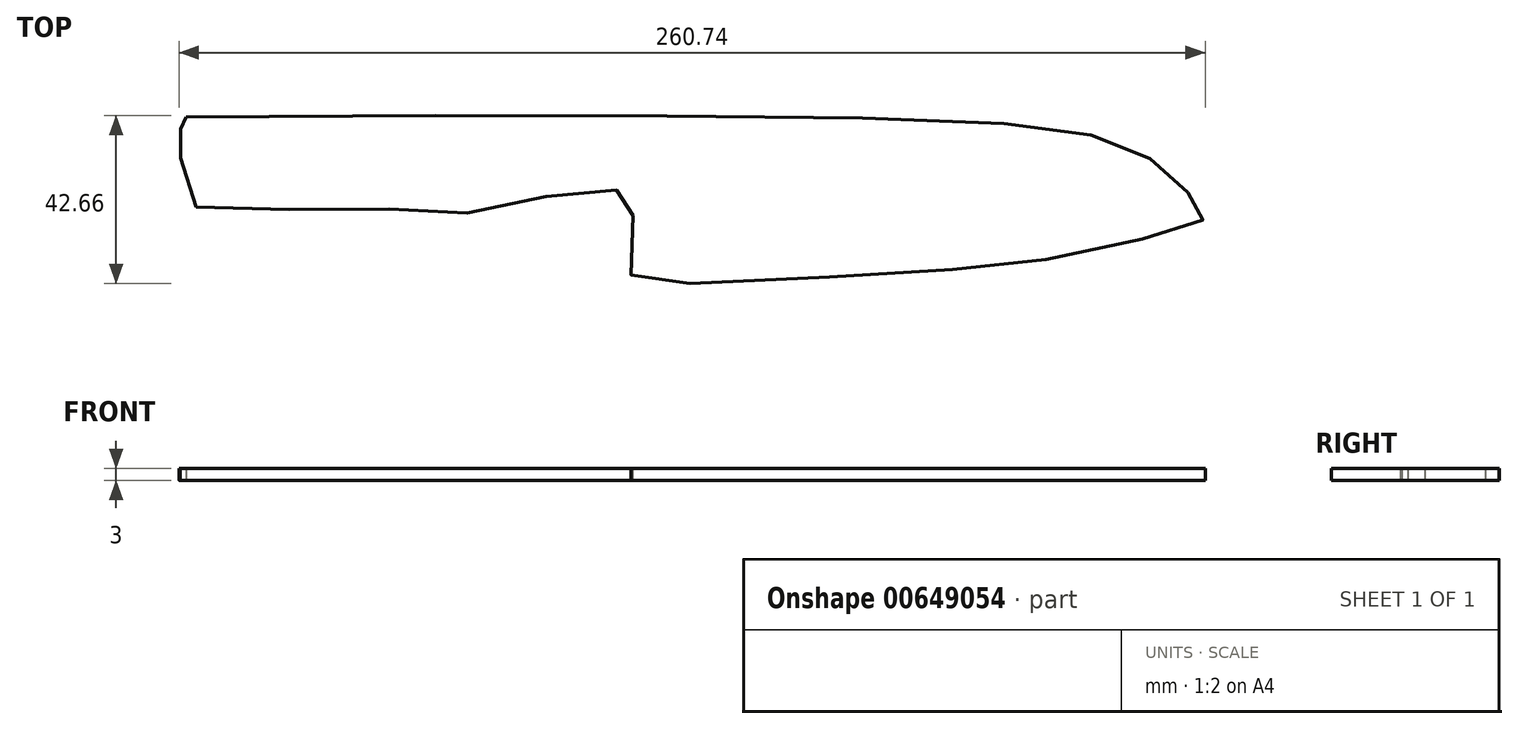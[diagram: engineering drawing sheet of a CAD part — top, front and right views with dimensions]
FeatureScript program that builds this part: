
annotation { "Feature Type Name" : "Feature", "Feature Type Description" : "" }
export const myFeature = defineFeature(function(context is Context, id is Id, definition is map)
    precondition{}
    {
        {
            var Q0;
            Q0=qCreatedBy(makeId("Top.planeOp"),FACE);
            var sketch = newSketch(context, id + "F0", { "sketchPlane" : qUnion([Q0])});
            skFitSpline(sketch, "E0", {"points": [v(-153.83, 13.17) * mm, v(44.72, 12) * mm, v(80.75, 7.17) * mm, v(94.73, 0) * mm, v(101.95, -7.6) * mm, v(105.12, -12.1) * mm, v(101.52, -14.35) * mm, v(67.78, -22.56) * mm, v(21.87, -26.75) * mm, v(-39.8, -28.3) * mm, v(-40.72, -25.6) * mm, v(-40.31, -8.96) * mm, v(-41.22, -6.26) * mm, v(-56.08, -5.86) * mm, v(-83.98, -11.35) * mm, v(-115.05, -9.65) * mm, v(-153.32, -8.42) * mm, v(-155.16, 3.72) * mm, v(-155.62, 8.22) * mm, v(-155.17, 10.02) * mm], "startDerivative": vector(1475.38, 7.35) * mm, "endDerivative": vector(41.7, 108.9) * mm});
            skLineSegment(sketch, "E1", {"start": v(-153.83, 13.17) * mm, "end": v(-155.17, 10.02) * mm});
            skSolve(sketch);
        }
        {
            var Q0;
            Q0 = qSketchRegion(id + "F0", true);
            extrude(context, id + "F1", {"entities" : qUnion([Q0]), "depth" : 3 * mm, "offsetDistance" : 25.4 * mm});
        }
    });
